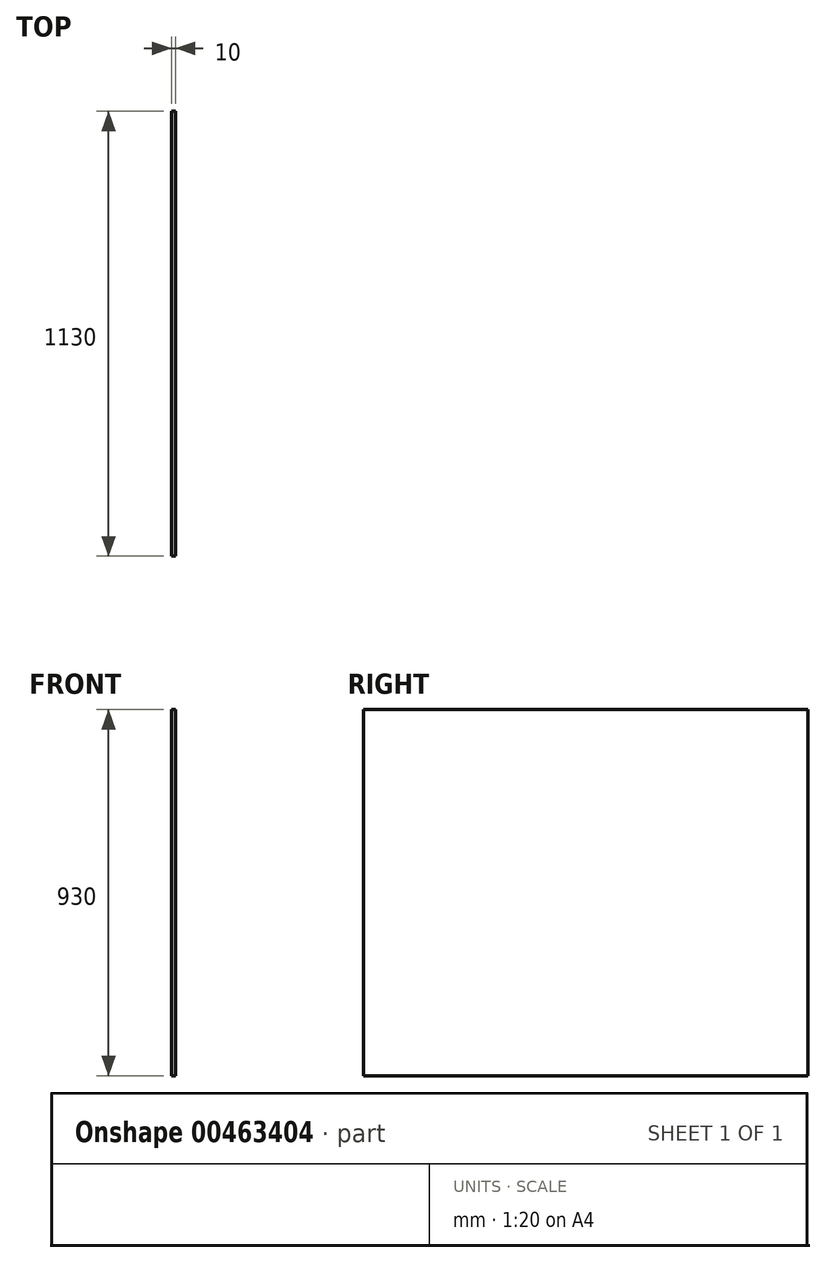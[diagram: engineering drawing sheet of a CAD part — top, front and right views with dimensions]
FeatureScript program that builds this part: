
annotation { "Feature Type Name" : "Feature", "Feature Type Description" : "" }
export const myFeature = defineFeature(function(context is Context, id is Id, definition is map)
    precondition{}
    {
        {
            var Q0;
            Q0=qCreatedBy(makeId("Front.planeOp"),FACE);
            var sketch = newSketch(context, id + "F0", { "sketchPlane" : qUnion([Q0])});
            skLineSegment(sketch, "E0.bottom", {"start": v(-54.98, 457.76) * mm, "end": v(-44.98, 457.76) * mm});
            skLineSegment(sketch, "E0.top", {"start": v(-54.98, -472.24) * mm, "end": v(-44.98, -472.24) * mm});
            skLineSegment(sketch, "E0.left", {"start": v(-54.98, 457.76) * mm, "end": v(-54.98, -472.24) * mm});
            skLineSegment(sketch, "E0.right", {"start": v(-44.98, 457.76) * mm, "end": v(-44.98, -472.24) * mm});
            skSolve(sketch);
        }
        {
            var Q0;
            Q0=makeQuery(id+"F0.imprint","IMPRINT",FACE,{"disambiguationData":[TD([[makeQuery(id+"F0.imprint","IMPRINT",EDGE,{"derivedFrom":sQuery(id+"F0.wireOp",EDGE,"E0.bottom")}),-1.0]])]});
            extrude(context, id + "F1", {"entities" : qUnion([Q0]), "oppositeDirection" : true, "depth" : 1130 * mm});
        }
    });
